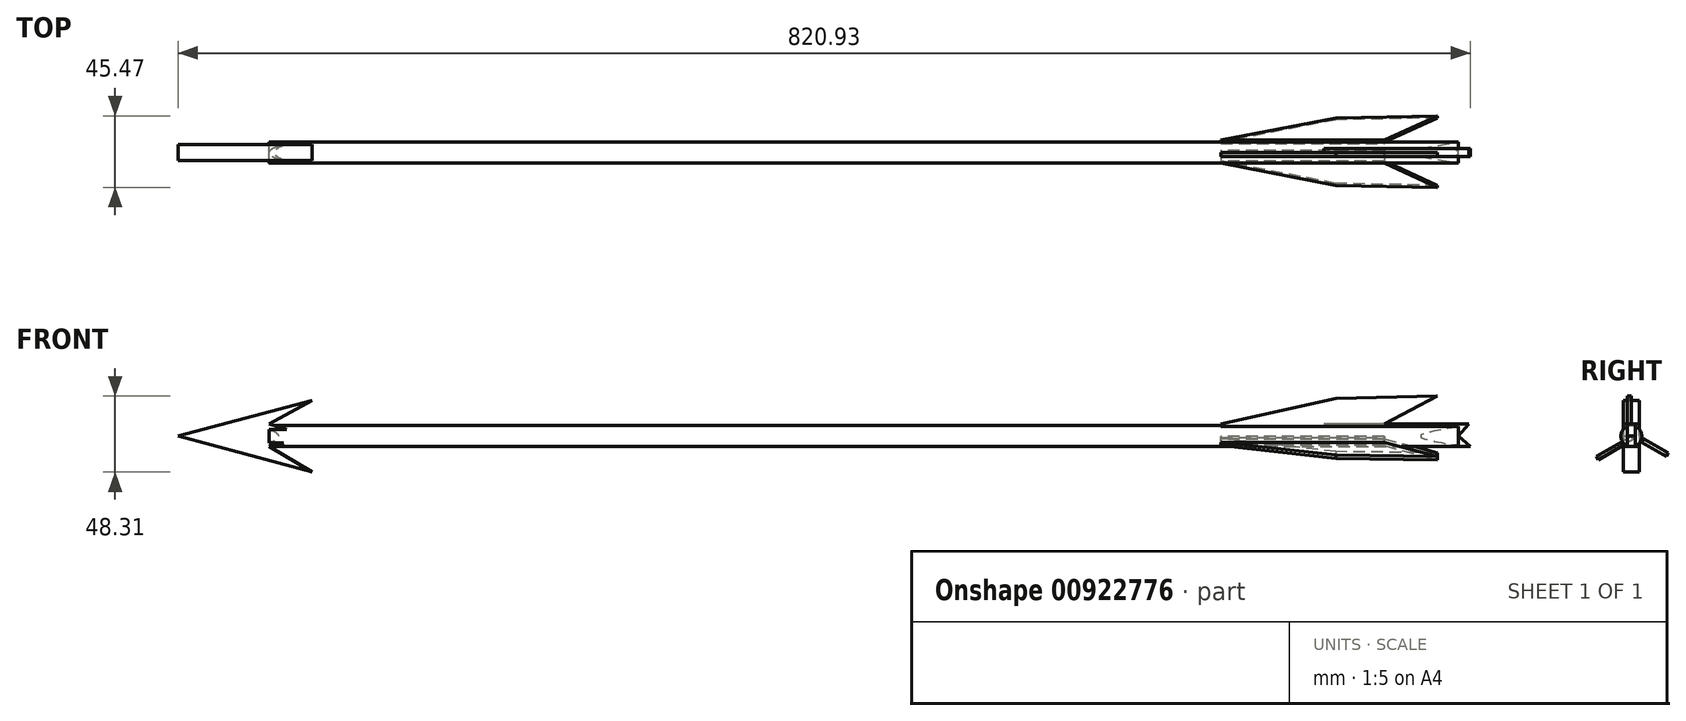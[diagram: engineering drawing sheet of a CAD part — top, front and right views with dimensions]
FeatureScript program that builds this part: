
annotation { "Feature Type Name" : "Feature", "Feature Type Description" : "" }
export const myFeature = defineFeature(function(context is Context, id is Id, definition is map)
    precondition{}
    {
        {
            var Q0;
            Q0=qCreatedBy(makeId("Front.planeOp"),FACE);
            var sketch = newSketch(context, id + "F0", { "sketchPlane" : qUnion([Q0])});
            skLineSegment(sketch, "E0", {"start": v(231.95, 0) * mm, "end": v(224.28, 6.66) * mm});
            skLineSegment(sketch, "E1", {"start": v(224.28, 6.66) * mm, "end": v(230.94, 14.33) * mm});
            skLineSegment(sketch, "E2", {"start": v(230.94, 14.33) * mm, "end": v(-531.06, 14.33) * mm});
            skLineSegment(sketch, "E3", {"start": v(-531.06, 0) * mm, "end": v(231.95, 0) * mm});
            skLineSegment(sketch, "E4", {"start": v(-531.06, 14.33) * mm, "end": v(-503.92, 29.45) * mm});
            skLineSegment(sketch, "E5", {"start": v(-588.98, 6.66) * mm, "end": v(-503.92, -16.13) * mm});
            skLineSegment(sketch, "E6", {"start": v(-503.92, -16.13) * mm, "end": v(-531.06, 0) * mm});
            skLineSegment(sketch, "E7", {"start": v(-588.98, 6.66) * mm, "end": v(-503.92, 29.45) * mm});
            skLineSegment(sketch, "E8", {"start": v(138.83, 14.33) * mm, "end": v(224.28, 0) * mm});
            skLineSegment(sketch, "E9", {"start": v(177.23, 14.33) * mm, "end": v(210.86, 32.18) * mm});
            skLineSegment(sketch, "E10", {"start": v(210.86, 32.18) * mm, "end": v(146.46, 30.69) * mm});
            skLineSegment(sketch, "E11", {"start": v(146.46, 30.69) * mm, "end": v(73.32, 14.33) * mm});
            skLineSegment(sketch, "E12", {"start": v(-531.06, 14.33) * mm, "end": v(-505.68, 6.66) * mm});
            skLineSegment(sketch, "E13", {"start": v(-505.68, 6.66) * mm, "end": v(-531.06, 0) * mm});
            skLineSegment(sketch, "E14", {"start": v(224.28, 6.66) * mm, "end": v(-505.68, 6.66) * mm});
            skLineSegment(sketch, "E15", {"start": v(-505.68, 6.66) * mm, "end": v(-503.92, 29.45) * mm, "construction": true});
            skLineSegment(sketch, "E16", {"start": v(-505.68, 6.66) * mm, "end": v(-503.92, -16.13) * mm, "construction": true});
            skSolve(sketch);
        }
        {
            var Q0;
            {var subQ1=sQuery(id+"F0.wireOp",EDGE,"E3");var subQ3=sQuery(id+"F0.wireOp",EDGE,"E8");var subQ4=makeQuery(id+"F0.imprint","INTERSECT",VERTEX,{"derivedFrom":[subQ1,subQ3]});Q0=makeQuery(id+"F0.imprint","IMPRINT",FACE,{"disambiguationData":[TD([[makeQuery(id+"F0.imprint","IMPRINT",EDGE,{"disambiguationData":[TD([[subQ4,1.0]])],"derivedFrom":subQ3}),-1.0]])]});}
            var Q1;
            Q1=sQuery(id+"F0.wireOp",EDGE,"E14");
            revolve(context, id + "F1", {"surfaceOperationType" : NewSurfaceOperationType.NEW, "entities" : qUnion([Q0]), "axis" : qUnion([Q1]), "revolveType" : RevolveType.FULL});
        }
        {
            var Q0;
            {var subQ1=sQuery(id+"F0.wireOp",EDGE,"E4");Q0=makeQuery(id+"F0.imprint","IMPRINT",FACE,{"disambiguationData":[TD([[makeQuery(id+"F0.imprint","IMPRINT",EDGE,{"derivedFrom":subQ1}),1.0]])]});}
            extrude(context, id + "F2", {"entities" : qUnion([Q0]), "depth" : 5.08 * mm, "offsetDistance" : 25.4 * mm});
        }
        {
            var Q0;
            {var subQ1=sQuery(id+"F0.wireOp",EDGE,"E4");Q0=makeQuery(id+"F0.imprint","IMPRINT",FACE,{"disambiguationData":[TD([[makeQuery(id+"F0.imprint","IMPRINT",EDGE,{"derivedFrom":subQ1}),1.0]])]});}
            extrude(context, id + "F3", {"entities" : qUnion([Q0]), "operationType" : NewBodyOperationType.ADD, "oppositeDirection" : true, "depth" : 5.08 * mm, "offsetDistance" : 25.4 * mm});
        }
        {
            var Q0;
            {var subQ0=sQuery(id+"F0.wireOp",EDGE,"E9");Q0=makeQuery(id+"F0.imprint","IMPRINT",FACE,{"disambiguationData":[TD([[makeQuery(id+"F0.imprint","IMPRINT",EDGE,{"derivedFrom":subQ0}),1.0]])]});}
            extrude(context, id + "F4", {"entities" : qUnion([Q0]), "depth" : 2.54 * mm, "offsetDistance" : 25.4 * mm});
        }
        {
            var Q0;
            Q0=makeQuery(id+"F4.opExtrude","SWEPT_BODY",BODY,{"disambiguationData":[OSD([sQuery(id+"F0.wireOp",EDGE,"E2"),sQuery(id+"F0.wireOp",EDGE,"E9"),sQuery(id+"F0.wireOp",EDGE,"E10"),sQuery(id+"F0.wireOp",EDGE,"E11")])]});
            var Q1;
            Q1=sQuery(id+"F0.wireOp",EDGE,"E14");
            circularPattern(context, id + "F5", {"entities" : qUnion([Q0]), "axis" : qUnion([Q1]), "angle" : 360 * degree, "instanceCount" : 3, "equalSpace" : true});
        }
        {
            var Q0;
            Q0=makeQuery(id+"F5.opPattern","COPY",FACE,{"derivedFrom":makeQuery(id+"F4.opExtrude","SWEPT_FACE",FACE,{"disambiguationData":[OSD([sQuery(id+"F0.wireOp",EDGE,"E2")])]}),"instanceName":"1"});
            extrude(context, id + "F6", {"entities" : qUnion([Q0]), "depth" : 10.16 * mm, "offsetDistance" : 25.4 * mm});
        }
        {
            var Q0;
            Q0=makeQuery(id+"F4.opExtrude","SWEPT_FACE",FACE,{"disambiguationData":[OSD([sQuery(id+"F0.wireOp",EDGE,"E2")])]});
            extrude(context, id + "F7", {"entities" : qUnion([Q0]), "depth" : 10.16 * mm, "offsetDistance" : 25.4 * mm});
        }
        {
            var Q0;
            Q0=makeQuery(id+"F5.opPattern","COPY",FACE,{"derivedFrom":makeQuery(id+"F4.opExtrude","SWEPT_FACE",FACE,{"disambiguationData":[OSD([sQuery(id+"F0.wireOp",EDGE,"E2")])]}),"instanceName":"2"});
            extrude(context, id + "F8", {"entities" : qUnion([Q0]), "depth" : 7.62 * mm, "offsetDistance" : 25.4 * mm});
        }
        {
            var Q0;
            {var subQ0=sQuery(id+"F0.wireOp",EDGE,"E1");Q0=makeQuery(id+"F0.imprint","IMPRINT",FACE,{"disambiguationData":[TD([[makeQuery(id+"F0.imprint","IMPRINT",EDGE,{"derivedFrom":subQ0}),1.0]])]});}
            var Q1;
            {var subQ0=sQuery(id+"F0.wireOp",EDGE,"E0");Q1=makeQuery(id+"F0.imprint","IMPRINT",FACE,{"disambiguationData":[TD([[makeQuery(id+"F0.imprint","IMPRINT",EDGE,{"derivedFrom":subQ0}),1.0]])]});}
            extrude(context, id + "F9", {"entities" : qUnion([Q0, Q1]), "operationType" : NewBodyOperationType.ADD, "depth" : 2.54 * mm, "offsetDistance" : 25.4 * mm, "hasSecondDirection" : true, "secondDirectionOppositeDirection" : true, "secondDirectionDepth" : 2.54 * mm});
        }
    });
